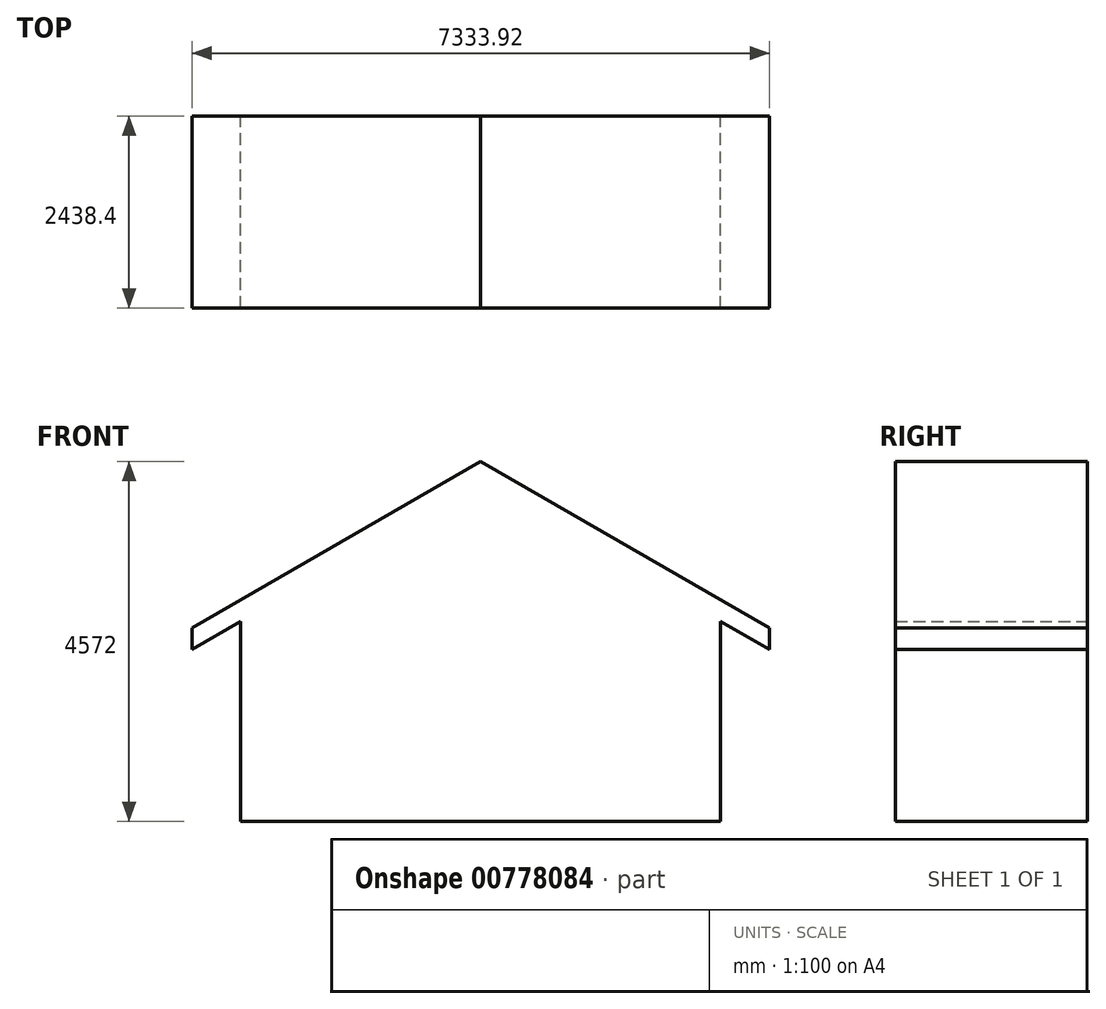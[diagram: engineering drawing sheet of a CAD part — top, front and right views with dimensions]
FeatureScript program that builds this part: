
annotation { "Feature Type Name" : "Feature", "Feature Type Description" : "" }
export const myFeature = defineFeature(function(context is Context, id is Id, definition is map)
    precondition{}
    {
        {
            var Q0;
            Q0=qCreatedBy(makeId("Front.planeOp"),FACE);
            var sketch = newSketch(context, id + "F0", { "sketchPlane" : qUnion([Q0])});
            skLineSegment(sketch, "E0", {"start": v(-3048, 0) * mm, "end": v(-3048, 2540) * mm});
            skLineSegment(sketch, "E1", {"start": v(-3048, 2540) * mm, "end": v(-3666.96, 2182.64) * mm});
            skLineSegment(sketch, "E2", {"start": v(-3666.96, 2182.64) * mm, "end": v(-3666.96, 2454.88) * mm});
            skLineSegment(sketch, "E3", {"start": v(-3666.96, 2454.88) * mm, "end": v(0, 4572) * mm});
            skLineSegment(sketch, "E4", {"start": v(0, 4572) * mm, "end": v(0, 0) * mm, "construction": true});
            skLineSegment(sketch, "E5", {"start": v(0, 0) * mm, "end": v(-3048, 0) * mm});
            skLineSegment(sketch, "E6.MirrorCS", {"start": v(3666.96, 2454.88) * mm, "end": v(0, 4572) * mm});
            skLineSegment(sketch, "E7.MirrorCS", {"start": v(3666.96, 2182.64) * mm, "end": v(3666.96, 2454.88) * mm});
            skLineSegment(sketch, "E8.MirrorCS", {"start": v(3048, 2540) * mm, "end": v(3666.96, 2182.64) * mm});
            skLineSegment(sketch, "E9.MirrorCS", {"start": v(3048, 0) * mm, "end": v(3048, 2540) * mm});
            skLineSegment(sketch, "E10.MirrorCS", {"start": v(0, 0) * mm, "end": v(3048, 0) * mm});
            skSolve(sketch);
        }
        {
            var Q0;
            Q0 = qSketchRegion(id + "F0", true);
            extrude(context, id + "F1", {"entities" : qUnion([Q0]), "depth" : 2438.4 * mm, "offsetDistance" : 25.4 * mm});
        }
    });
